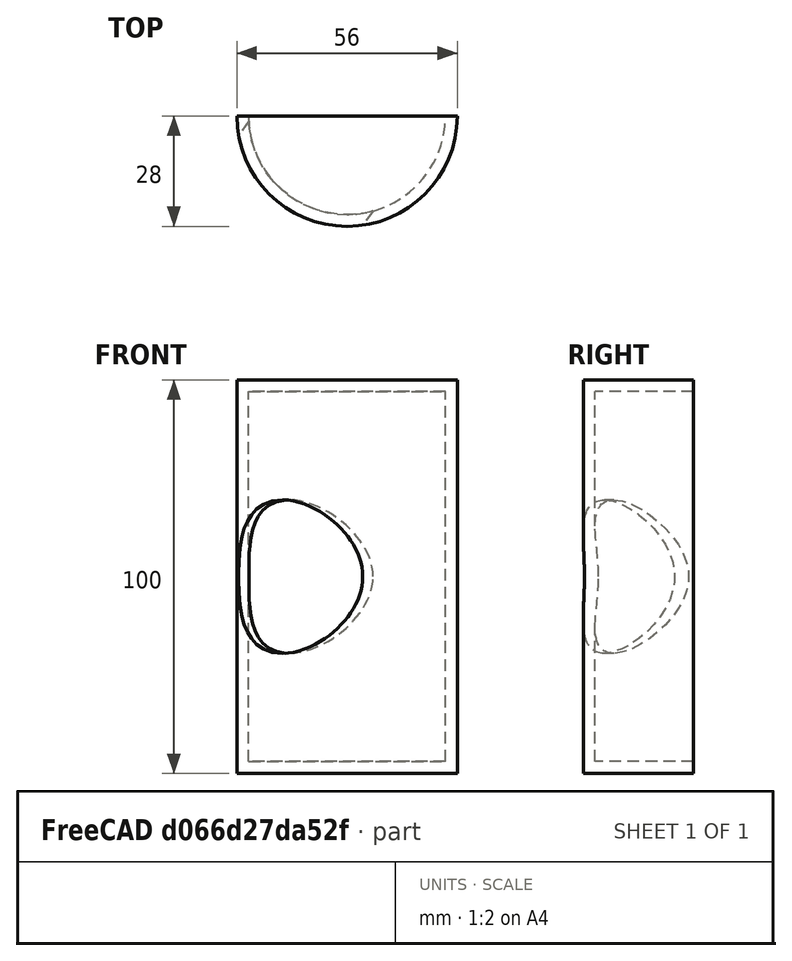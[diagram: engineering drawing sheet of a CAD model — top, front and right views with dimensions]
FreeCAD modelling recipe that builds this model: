
FCSTD DOCUMENT  (FreeCAD 0.18R4 (GitTag))
Label: augerHousing
License: All rights reserved
LicenseURL: http://en.wikipedia.org/wiki/All_rights_reserved
objects: PartDesign::SubtractiveCylinder×2, PartDesign::AdditiveCylinder×1, PartDesign::SubtractiveBox×1, PartDesign::Body×1, App::Part×1
note: 9 computed .brp shape members not serialized (recipe doc carries the construction recipe); baked Part::Feature solids carry a one-line shape summary decoded from their .brp

FEATURE [PartDesign::AdditiveCylinder] Cylinder
  Angle = 360
  AttacherType = Attacher::AttachEngine3D
  Height = 100
  MapMode = 2
  Radius = 28
  Support = -> [X_Axis001]
FEATURE [PartDesign::SubtractiveCylinder] Cylinder002
  Angle = 360
  AttacherType = Attacher::AttachEngine3D
  AttachmentOffset = pos=(0,0,3) rot=(0,0,1;0rad)
  BaseFeature = -> Cylinder
  Height = 94
  MapMode = 5
  Placement = pos=(0,0,3) rot=(0,0,1;0rad)
  Radius = 25
  Support = -> [XY_Plane001]
FEATURE [PartDesign::SubtractiveBox] Box
  AttacherType = Attacher::AttachEngine3D
  AttachmentOffset = pos=(-30,0,-11) rot=(0,0,1;0rad)
  BaseFeature = -> Cylinder002
  Height = 120
  Length = 60
  MapMode = 5
  Placement = pos=(-30,0,-11) rot=(0,0,1;0rad)
  Support = -> [XY_Plane001]
  Width = 30
FEATURE [PartDesign::SubtractiveCylinder] Cylinder003
  Angle = 360
  AttacherType = Attacher::AttachEngine3D
  AttachmentOffset = pos=(0,0,50) rot=(0.908661,-0.295242,-0.295242;1.66643rad)
  BaseFeature = -> Box
  Height = 30
  MapMode = 5
  Placement = pos=(0,0,50) rot=(0.908661,-0.295242,-0.295242;1.66643rad)
  Radius = 19.5
  Support = -> [XY_Plane001]
FEATURE [PartDesign::Body] Body
  Group = -> [Cylinder,Cylinder002,Box,Cylinder003]
  Origin = -> Origin001
  Tip = -> Cylinder003
FEATURE [App::Part] Part
  Group = -> [Body]
  Origin = -> Origin
